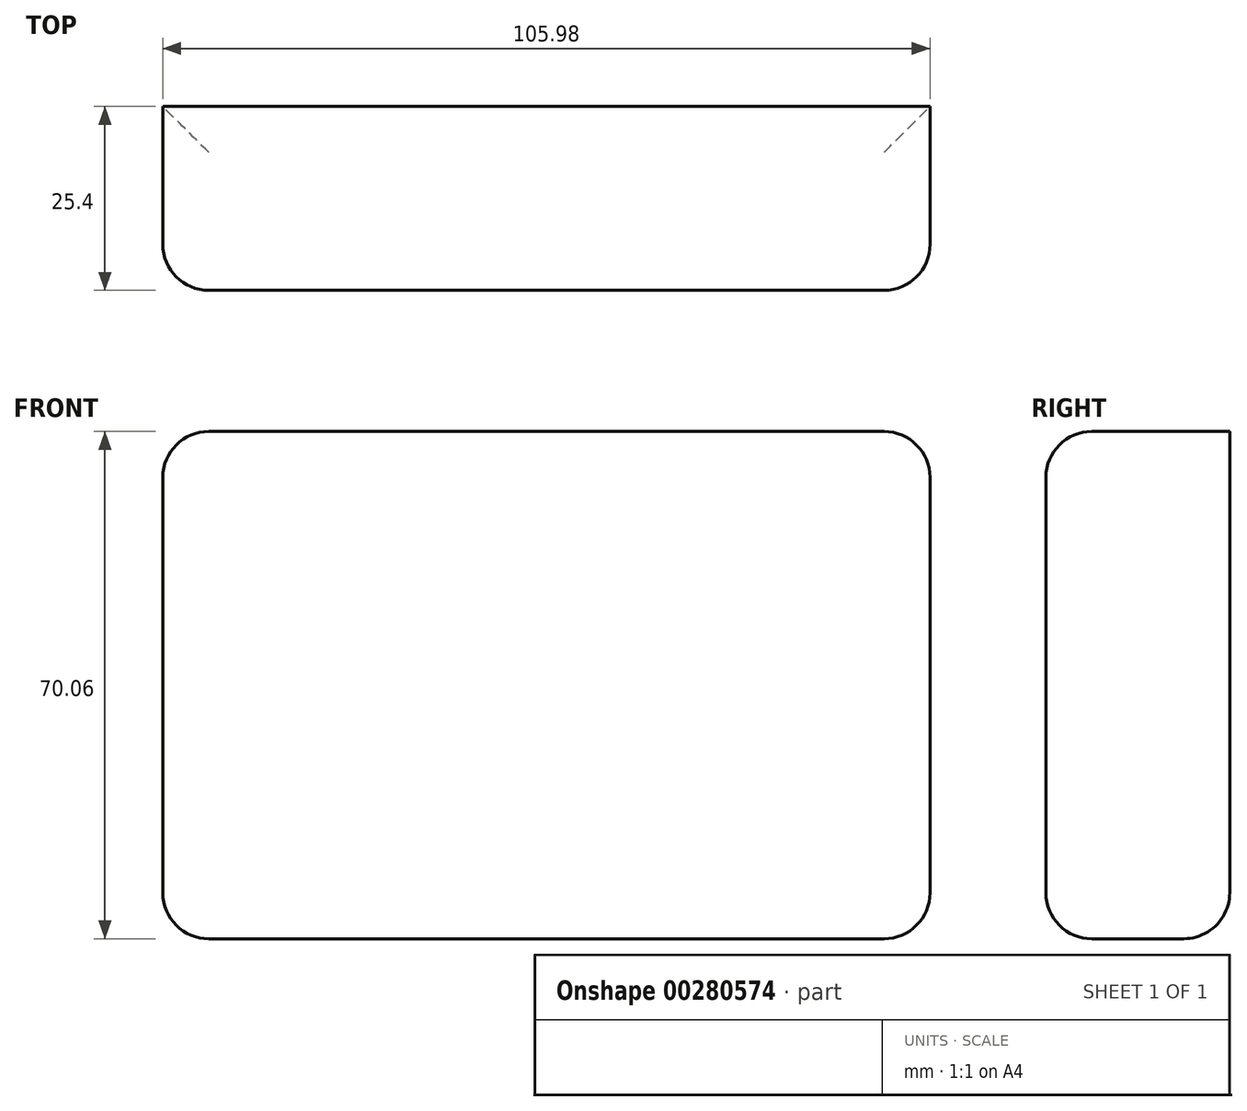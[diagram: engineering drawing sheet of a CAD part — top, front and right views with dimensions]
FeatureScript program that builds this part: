
annotation { "Feature Type Name" : "Feature", "Feature Type Description" : "" }
export const myFeature = defineFeature(function(context is Context, id is Id, definition is map)
    precondition{}
    {
        {
            var Q0;
            Q0=qCreatedBy(makeId("Front.planeOp"),FACE);
            var sketch = newSketch(context, id + "F0", { "sketchPlane" : qUnion([Q0])});
            skLineSegment(sketch, "E0.bottom", {"start": v(-52.99, 35.03) * mm, "end": v(52.99, 35.03) * mm});
            skLineSegment(sketch, "E0.top", {"start": v(-52.99, -35.03) * mm, "end": v(52.99, -35.03) * mm});
            skLineSegment(sketch, "E0.left", {"start": v(-52.99, 35.03) * mm, "end": v(-52.99, -35.03) * mm});
            skLineSegment(sketch, "E0.right", {"start": v(52.99, 35.03) * mm, "end": v(52.99, -35.03) * mm});
            skPoint(sketch, "E0.middle", {"position": v(0, 0) * mm});
            skSolve(sketch);
        }
        {
            var Q0;
            Q0 = qSketchRegion(id + "F0", true);
            extrude(context, id + "F1", {"entities" : qUnion([Q0]), "depth" : 25.4 * mm});
        }
        {
            var Q0;
            Q0=makeQuery(id+"F1.opExtrude","CAP_EDGE",EDGE,{"disambiguationData":[OSD([sQuery(id+"F0.wireOp",EDGE,"E0.bottom")])],"isStart":false});
            var Q1;
            Q1=makeQuery(id+"F1.opExtrude","CAP_FACE",FACE,{"disambiguationData":[OSD([sQuery(id+"F0.wireOp",EDGE,"E0.bottom"),sQuery(id+"F0.wireOp",EDGE,"E0.top"),sQuery(id+"F0.wireOp",EDGE,"E0.left"),sQuery(id+"F0.wireOp",EDGE,"E0.right")])],"isStart":false});
            var Q2;
            Q2=makeQuery(id+"F1.opExtrude","SWEPT_EDGE",EDGE,{"disambiguationData":[OSD([sQuery(id+"F0.wireOp",EDGE,"E0.top"),sQuery(id+"F0.wireOp",EDGE,"E0.right")])]});
            var Q3;
            Q3=makeQuery(id+"F1.opExtrude","SWEPT_EDGE",EDGE,{"disambiguationData":[OSD([sQuery(id+"F0.wireOp",EDGE,"E0.bottom"),sQuery(id+"F0.wireOp",EDGE,"E0.right")])]});
            var Q4;
            Q4=makeQuery(id+"F1.opExtrude","CAP_EDGE",EDGE,{"disambiguationData":[OSD([sQuery(id+"F0.wireOp",EDGE,"E0.top")])],"isStart":true});
            var Q5;
            Q5=makeQuery(id+"F1.opExtrude","SWEPT_EDGE",EDGE,{"disambiguationData":[OSD([sQuery(id+"F0.wireOp",EDGE,"E0.top"),sQuery(id+"F0.wireOp",EDGE,"E0.left")])]});
            var Q6;
            Q6=makeQuery(id+"F1.opExtrude","SWEPT_EDGE",EDGE,{"disambiguationData":[OSD([sQuery(id+"F0.wireOp",EDGE,"E0.bottom"),sQuery(id+"F0.wireOp",EDGE,"E0.left")])]});
            fillet(context, id + "F2", {"entities" : qUnion([Q0, Q1, Q2, Q3, Q4, Q5, Q6]), "radius" : 6.35 * mm, "allowEdgeOverflow" : false});
        }
    });
